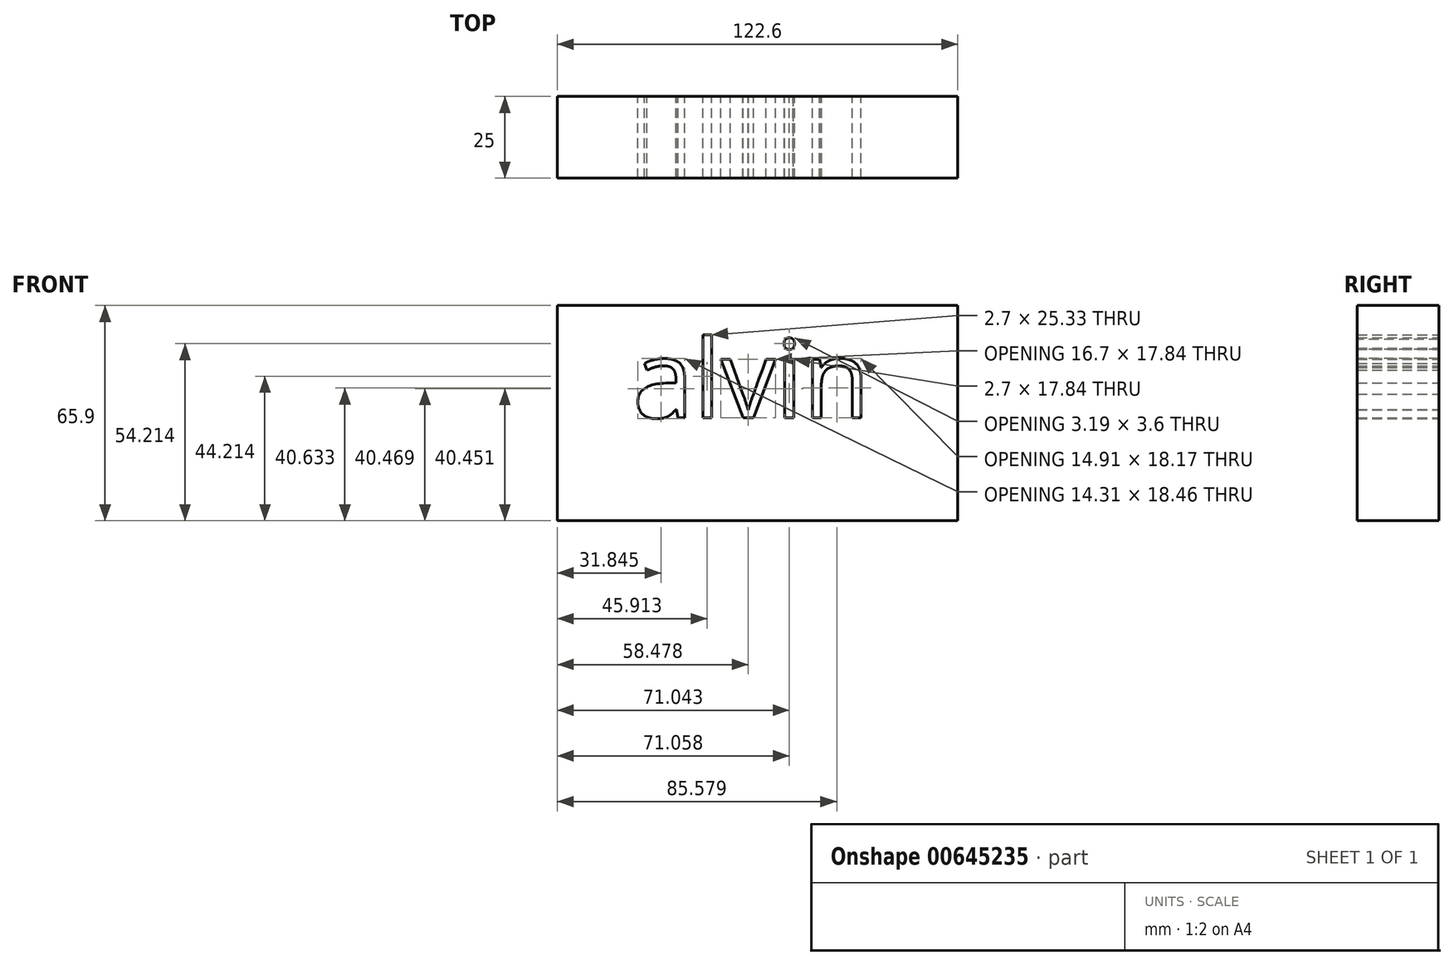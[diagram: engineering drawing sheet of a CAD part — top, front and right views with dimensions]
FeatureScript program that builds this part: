
annotation { "Feature Type Name" : "Feature", "Feature Type Description" : "" }
export const myFeature = defineFeature(function(context is Context, id is Id, definition is map)
    precondition{}
    {
        {
            var Q0;
            Q0=qCreatedBy(makeId("Front.planeOp"),FACE);
            var sketch = newSketch(context, id + "F0", { "sketchPlane" : qUnion([Q0])});
            skLineSegment(sketch, "E0.bottom", {"start": v(-148.5, 105) * mm, "end": v(148.5, 105) * mm});
            skLineSegment(sketch, "E0.top", {"start": v(-148.5, -105) * mm, "end": v(148.5, -105) * mm});
            skLineSegment(sketch, "E0.left", {"start": v(-148.5, 105) * mm, "end": v(-148.5, -105) * mm});
            skLineSegment(sketch, "E0.right", {"start": v(148.5, 105) * mm, "end": v(148.5, -105) * mm});
            skPoint(sketch, "E0.middle", {"position": v(0, 0) * mm});
            skSolve(sketch);
        }
        {
            var Q0;
            Q0=makeQuery(id+"F0.imprint","IMPRINT",FACE,{"disambiguationData":[TD([[makeQuery(id+"F0.imprint","IMPRINT",EDGE,{"derivedFrom":sQuery(id+"F0.wireOp",EDGE,"E0.bottom")}),-1.0]])]});
            var sketch = newSketch(context, id + "F1", { "sketchPlane" : qUnion([Q0])});
            skLineSegment(sketch, "E1.bottom", {"start": v(0, 0) * mm, "end": v(122.6, 0) * mm});
            skLineSegment(sketch, "E1.top", {"start": v(0, 65.9) * mm, "end": v(122.6, 65.9) * mm});
            skLineSegment(sketch, "E1.left", {"start": v(0, 0) * mm, "end": v(0, 65.9) * mm});
            skLineSegment(sketch, "E1.right", {"start": v(122.6, 0) * mm, "end": v(122.6, 65.9) * mm});
            skText(sketch, "E2", { "text": "alvin", "fontName": "OpenSans-Regular.ttf"});
            const initialGuessF1  = {"E2": [0.02316, 0.03155, 1, 0, 0.024]};
            skSetInitialGuess(sketch, initialGuessF1);
            skSolve(sketch);
        }
        {
            var Q0;
            Q0 = qSketchRegion(id + "F1", true);
            extrude(context, id + "F2", {"entities" : qUnion([Q0]), "depth" : 25 * mm, "offsetDistance" : 25 * mm});
        }
    });
